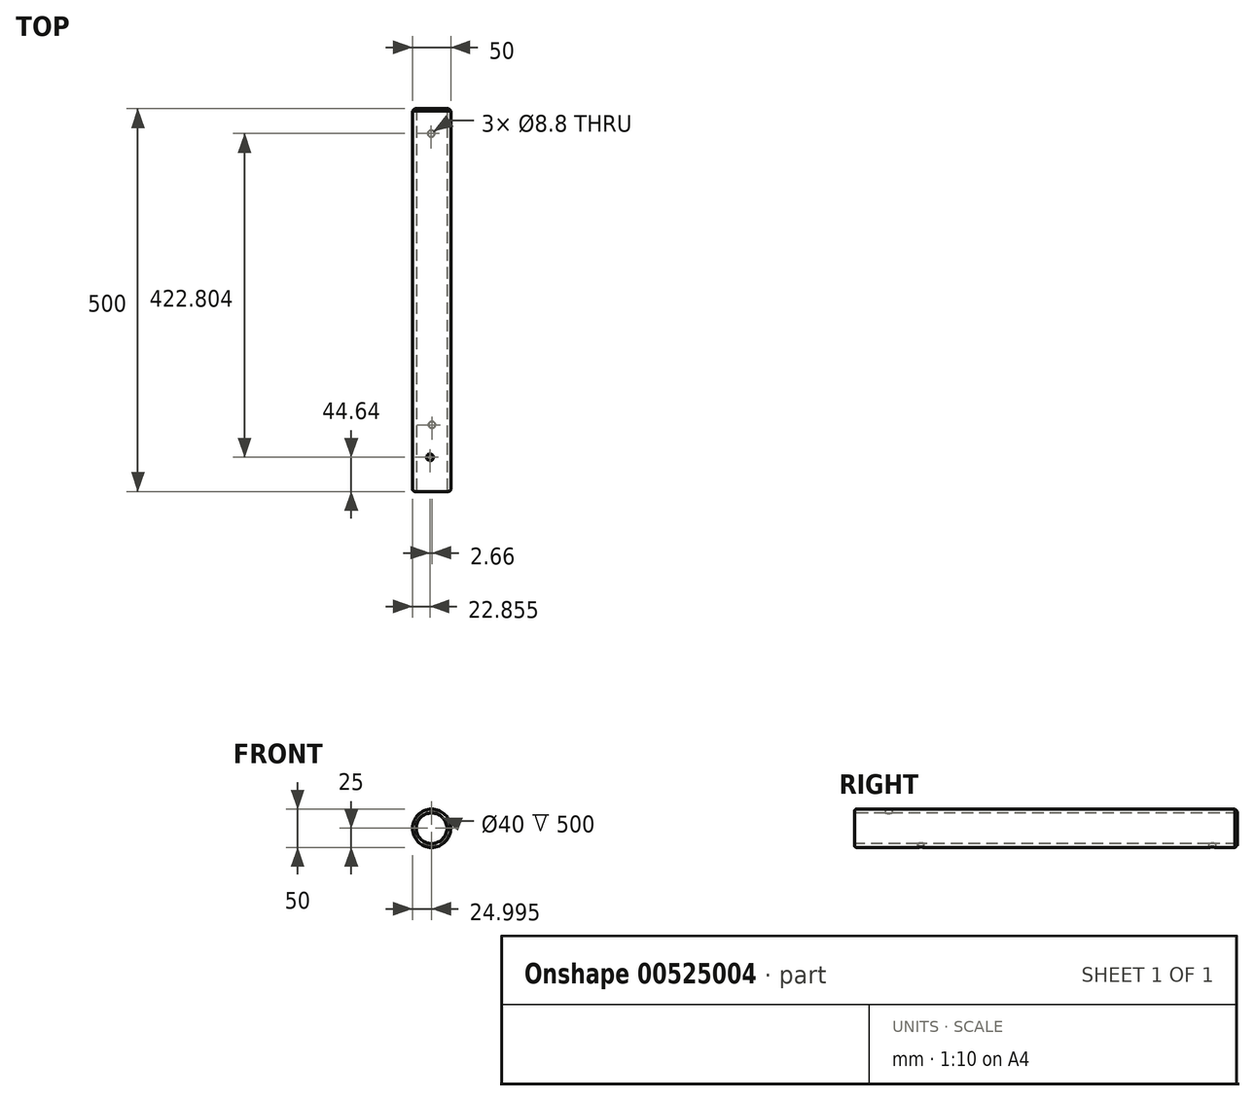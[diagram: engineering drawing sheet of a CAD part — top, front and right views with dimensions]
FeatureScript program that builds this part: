
annotation { "Feature Type Name" : "Feature", "Feature Type Description" : "" }
export const myFeature = defineFeature(function(context is Context, id is Id, definition is map)
    precondition{}
    {
        {
            var Q0;
            Q0=qCreatedBy(makeId("Front.planeOp"),FACE);
            var sketch = newSketch(context, id + "F0", { "sketchPlane" : qUnion([Q0])});
            skCircle(sketch, "E0", {"center": v(-44.65, 0) * mm, "radius": 25 * mm});
            skSolve(sketch);
        }
        {
            var Q0;
            Q0=makeQuery(id+"F0.imprint","IMPRINT",FACE,{"disambiguationData":[TD([[makeQuery(id+"F0.imprint","IMPRINT",EDGE,{"derivedFrom":sQuery(id+"F0.wireOp",EDGE,"E0")}),1.0]])]});
            extrude(context, id + "F1", {"entities" : qUnion([Q0]), "endBound" : BoundingType.SYMMETRIC, "oppositeDirection" : true, "depth" : 500 * mm, "offsetDistance" : 25 * mm});
        }
        {
            var Q0;
            Q0=makeQuery(id+"F1.opExtrude","CAP_FACE",FACE,{"disambiguationData":[OSD([sQuery(id+"F0.wireOp",EDGE,"E0")])],"isStart":true});
            var sketch = newSketch(context, id + "F2", { "sketchPlane" : qUnion([Q0])});
            skPoint(sketch, "E1", {"position": v(-44.65, 0) * mm});
            skSolve(sketch);
        }
        {
            var Q0;
            Q0=sQuery(id+"F2.wireOp",VERTEX,"E1");
            var Q1;
            Q1=makeQuery(id+"F1.opExtrude","SWEPT_BODY",BODY,{"disambiguationData":[OSD([sQuery(id+"F0.wireOp",EDGE,"E0")])]});
            hole(context, id + "F3", {"style" : HoleStyle.SIMPLE, "endStyle" : HoleEndStyle.THROUGH, "holeDiameter" : 40 * mm, "isTappedThrough" : true, "tappedDepth" : 12 * mm, "tapClearance" : 3, "startFromSketch" : true, "locations" : qUnion([Q0]), "scope" : qUnion([Q1])});
        }
        {
            var Q0;
            Q0=makeQuery(id+"F1.opExtrude","CAP_EDGE",EDGE,{"disambiguationData":[OSD([sQuery(id+"F0.wireOp",EDGE,"E0")])],"isStart":true});
            fillet(context, id + "F4", {"entities" : qUnion([Q0]), "radius" : 3 * mm, "tangentPropagation" : true, "allowEdgeOverflow" : false});
        }
        {
            var Q0;
            Q0=makeQuery(id+"F1.opExtrude","CAP_EDGE",EDGE,{"disambiguationData":[OSD([sQuery(id+"F0.wireOp",EDGE,"E0")])],"isStart":false});
            chamfer(context, id + "F5", {"entities" : qUnion([Q0]), "width" : 3 * mm, "tangentPropagation" : true});
        }
        {
            var Q0;
            Q0=qCreatedBy(makeId("Top.planeOp"),FACE);
            var sketch = newSketch(context, id + "F6", { "sketchPlane" : qUnion([Q0])});
            skPoint(sketch, "E2", {"position": v(-45.1, 217.44) * mm});
            skSolve(sketch);
        }
        {
            var Q0;
            Q0=sQuery(id+"F6.wireOp",VERTEX,"E2");
            var Q1;
            Q1=makeQuery(id+"F1.opExtrude","SWEPT_BODY",BODY,{"disambiguationData":[OSD([sQuery(id+"F0.wireOp",EDGE,"E0")])]});
            hole(context, id + "F7", {"style" : HoleStyle.SIMPLE, "endStyle" : HoleEndStyle.THROUGH, "standardTappedOrClearance" : lookupTablePath({ "standard" : "ISO", "fit" : "Normal", "size" : "M8", "type" : "Clearance" }), "standardBlindInLast" : lookupTablePath({ "fit" : "Standard", "standard" : "ISO", "size" : "M8", "type" : "Clearance" }), "holeDiameter" : 8.8 * mm, "isTappedThrough" : true, "tappedDepth" : 12 * mm, "tapClearance" : 3, "startFromSketch" : true, "locations" : qUnion([Q0]), "scope" : qUnion([Q1])});
        }
        {
            var Q0;
            Q0=qCreatedBy(makeId("Top.planeOp"),FACE);
            var sketch = newSketch(context, id + "F8", { "sketchPlane" : qUnion([Q0])});
            skPoint(sketch, "E3", {"position": v(-46.8, -205.36) * mm});
            skSolve(sketch);
        }
        {
            var Q0;
            Q0=sQuery(id+"F8.wireOp",VERTEX,"E3");
            var Q1;
            Q1=makeQuery(id+"F1.opExtrude","SWEPT_BODY",BODY,{"disambiguationData":[OSD([sQuery(id+"F0.wireOp",EDGE,"E0")])]});
            hole(context, id + "F9", {"style" : HoleStyle.SIMPLE, "endStyle" : HoleEndStyle.THROUGH, "oppositeDirection" : true, "standardTappedOrClearance" : lookupTablePath({ "standard" : "ISO", "fit" : "Normal", "size" : "M8", "type" : "Clearance" }), "standardBlindInLast" : lookupTablePath({ "fit" : "Standard", "standard" : "ISO", "size" : "M8", "type" : "Clearance" }), "holeDiameter" : 8.8 * mm, "isTappedThrough" : true, "tappedDepth" : 12 * mm, "tapClearance" : 3, "startFromSketch" : true, "locations" : qUnion([Q0]), "scope" : qUnion([Q1])});
        }
        {
            var Q0;
            Q0=qCreatedBy(makeId("Top.planeOp"),FACE);
            var sketch = newSketch(context, id + "F10", { "sketchPlane" : qUnion([Q0])});
            skPoint(sketch, "E4", {"position": v(-44.14, -163) * mm});
            skSolve(sketch);
        }
        {
            var Q0;
            Q0=sQuery(id+"F10.wireOp",VERTEX,"E4");
            var Q1;
            Q1=makeQuery(id+"F1.opExtrude","SWEPT_BODY",BODY,{"disambiguationData":[OSD([sQuery(id+"F0.wireOp",EDGE,"E0")])]});
            hole(context, id + "F11", {"style" : HoleStyle.C_BORE, "endStyle" : HoleEndStyle.THROUGH, "standardTappedOrClearance" : lookupTablePath({ "standard" : "ISO", "fit" : "Normal", "size" : "M8", "type" : "Clearance" }), "standardBlindInLast" : lookupTablePath({ "fit" : "Standard", "standard" : "ISO", "size" : "M8", "type" : "Clearance" }), "holeDiameter" : 8.8 * mm, "cBoreDiameter" : 14.25 * mm, "cBoreDepth" : 8 * mm, "isTappedThrough" : true, "tappedDepth" : 12 * mm, "tapClearance" : 3, "startFromSketch" : true, "locations" : qUnion([Q0]), "scope" : qUnion([Q1])});
        }
    });
